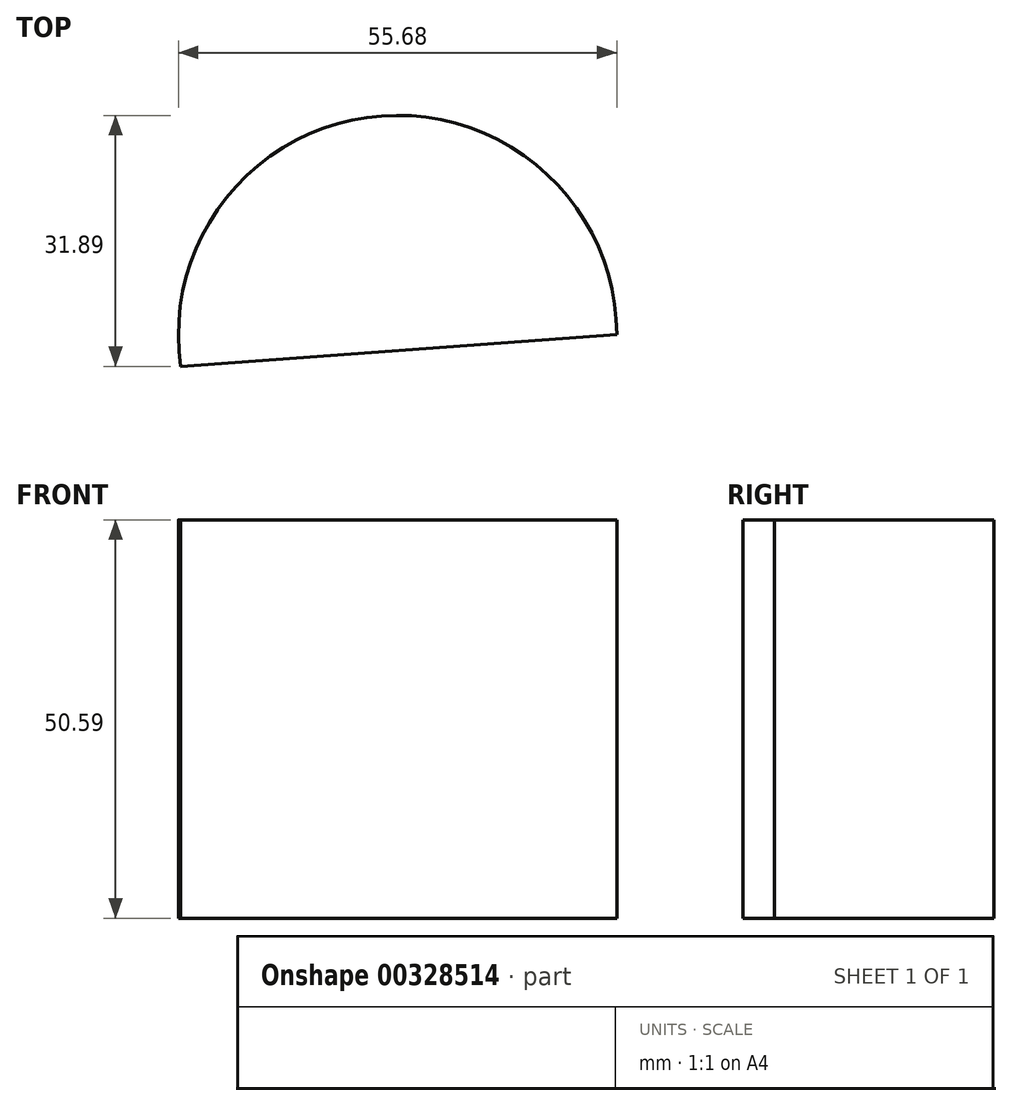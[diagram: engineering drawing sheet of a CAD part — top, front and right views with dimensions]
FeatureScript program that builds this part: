
annotation { "Feature Type Name" : "Feature", "Feature Type Description" : "" }
export const myFeature = defineFeature(function(context is Context, id is Id, definition is map)
    precondition{}
    {
        {
            var Q0;
            Q0=qCreatedBy(makeId("Top.planeOp"),FACE);
            var sketch = newSketch(context, id + "F0", { "sketchPlane" : qUnion([Q0])});
            skLineSegment(sketch, "E0.bottom", {"start": v(-43.33, 0) * mm, "end": v(-63.33, 0) * mm});
            skLineSegment(sketch, "E0.top", {"start": v(-43.33, -20) * mm, "end": v(-63.33, -20) * mm});
            skLineSegment(sketch, "E0.left", {"start": v(-43.33, 0) * mm, "end": v(-43.33, -20) * mm});
            skLineSegment(sketch, "E0.right", {"start": v(-63.33, 0) * mm, "end": v(-63.33, -20) * mm});
            skPoint(sketch, "E0.middle", {"position": v(-53.33, -10) * mm});
            skCircle(sketch, "E1", {"center": v(0, 0) * mm, "radius": 27.84 * mm});
            skLineSegment(sketch, "E2", {"start": v(-26.68, -7.94) * mm, "end": v(27.84, 0) * mm});
            skLineSegment(sketch, "E3", {"start": v(27.84, 0) * mm, "end": v(-31.4, -4.33) * mm});
            skLineSegment(sketch, "E4", {"start": v(-31.4, -4.33) * mm, "end": v(-27.6, 0.54) * mm});
            skSolve(sketch);
        }
        {
            var Q0;
            {var subQ1=sQuery(id+"F0.wireOp",EDGE,"E1");var subQ3=makeQuery(id+"F0.imprint","INTERSECT",VERTEX,{"derivedFrom":[subQ1,sQuery(id+"F0.wireOp",EDGE,"E4")]});Q0=makeQuery(id+"F0.imprint","IMPRINT",FACE,{"disambiguationData":[TD([[makeQuery(id+"F0.imprint","IMPRINT",EDGE,{"disambiguationData":[TD([[subQ3,-1.0]])],"derivedFrom":subQ1}),1.0]])]});}
            extrude(context, id + "F1", {"entities" : qUnion([Q0]), "depth" : 50.6 * mm});
        }
    });
